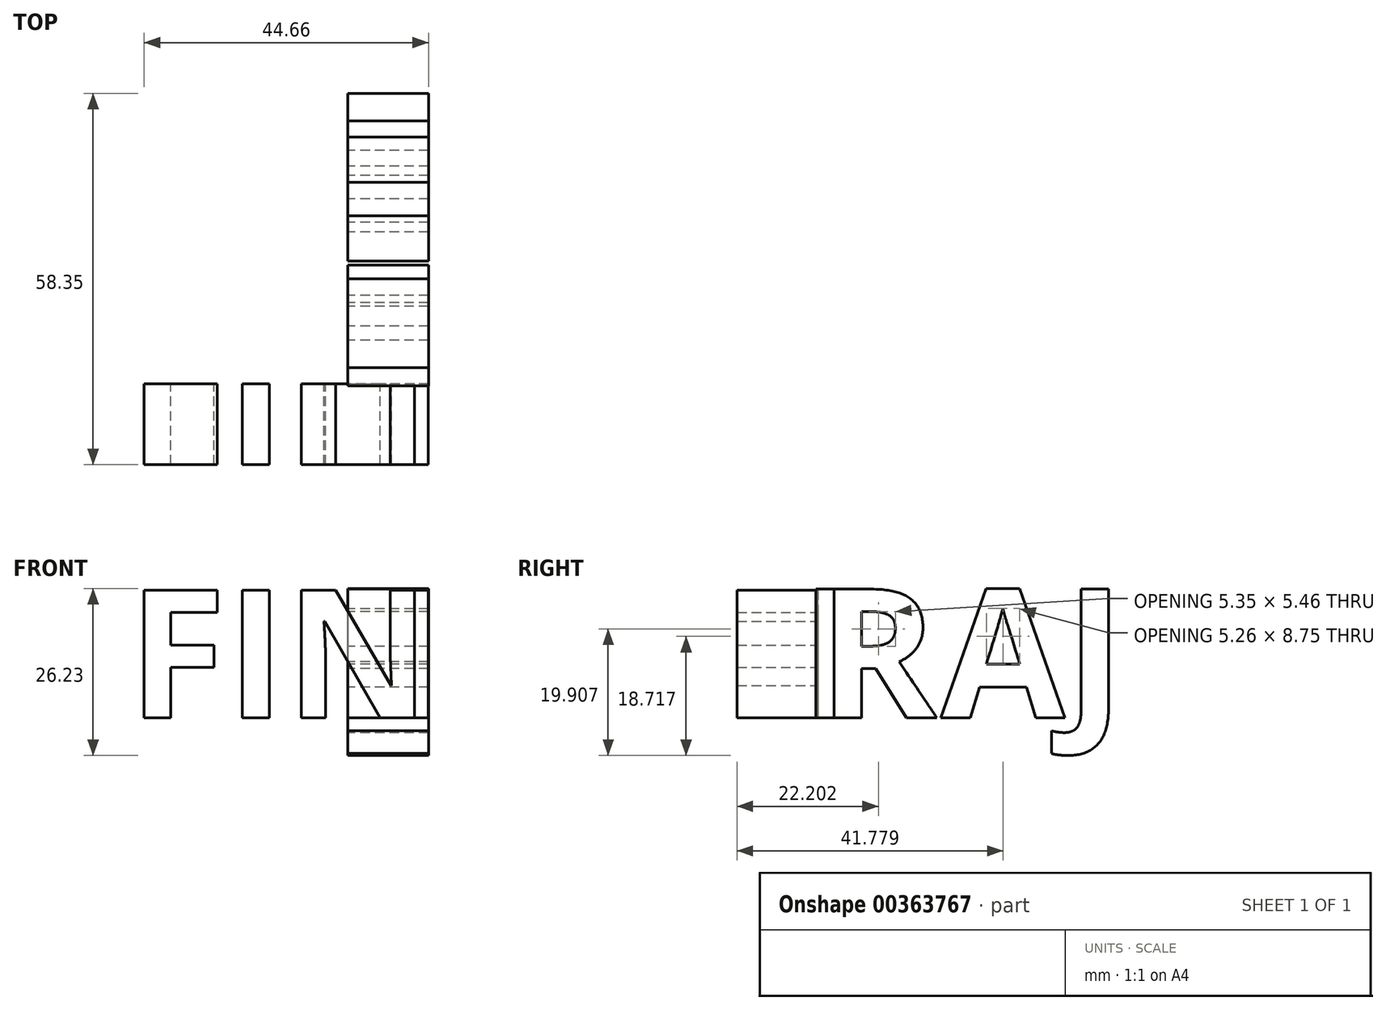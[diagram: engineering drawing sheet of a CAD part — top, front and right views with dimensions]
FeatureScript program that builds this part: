
annotation { "Feature Type Name" : "Feature", "Feature Type Description" : "" }
export const myFeature = defineFeature(function(context is Context, id is Id, definition is map)
    precondition{}
    {
        {
            var Q0;
            Q0=qCreatedBy(makeId("Front.planeOp"),FACE);
            var sketch = newSketch(context, id + "F0", { "sketchPlane" : qUnion([Q0])});
            skText(sketch, "E0", { "text": "FIN", "fontName": "OpenSans-Bold.ttf"});
            const initialGuessF0  = {"E0": [-0.03448, 0, 1, 0, 0.02021]};
            skSetInitialGuess(sketch, initialGuessF0);
            skSolve(sketch);
        }
        {
            var Q0;
            Q0=qCreatedBy(makeId("Right.planeOp"),FACE);
            var sketch = newSketch(context, id + "F1", { "sketchPlane" : qUnion([Q0])});
            skText(sketch, "E1", { "text": "RAJ", "fontName": "OpenSans-Bold.ttf"});
            const initialGuessF1  = {"E1": [0, 0, 1, 0, 0.02038]};
            skSetInitialGuess(sketch, initialGuessF1);
            skSolve(sketch);
        }
        {
            var Q0;
            Q0 = qSketchRegion(id + "F0", true);
            extrude(context, id + "F2", {"entities" : qUnion([Q0]), "depth" : 12.7 * mm});
        }
        {
            var Q0;
            Q0 = qSketchRegion(id + "F1", true);
            extrude(context, id + "F3", {"entities" : qUnion([Q0]), "depth" : 12.7 * mm});
        }
        {
            var Q0;
            Q0=makeQuery(id+"F3.opExtrude","SWEPT_FACE",FACE,{"disambiguationData":[OSD([sQuery(id+"F1.wireOp",EDGE,"E1.sketch_text.stroke-9")])]});
            extrude(context, id + "F4", {"entities" : qUnion([Q0]), "depth" : 2.84 * mm});
        }
        {
            var Q0;
            Q0=makeQuery(id+"F2.opExtrude","SWEPT_FACE",FACE,{"disambiguationData":[OSD([sQuery(id+"F0.wireOp",EDGE,"E0.sketch_text.stroke-27")])]});
            extrude(context, id + "F5", {"entities" : qUnion([Q0]), "depth" : 2.16 * mm});
        }
    });
